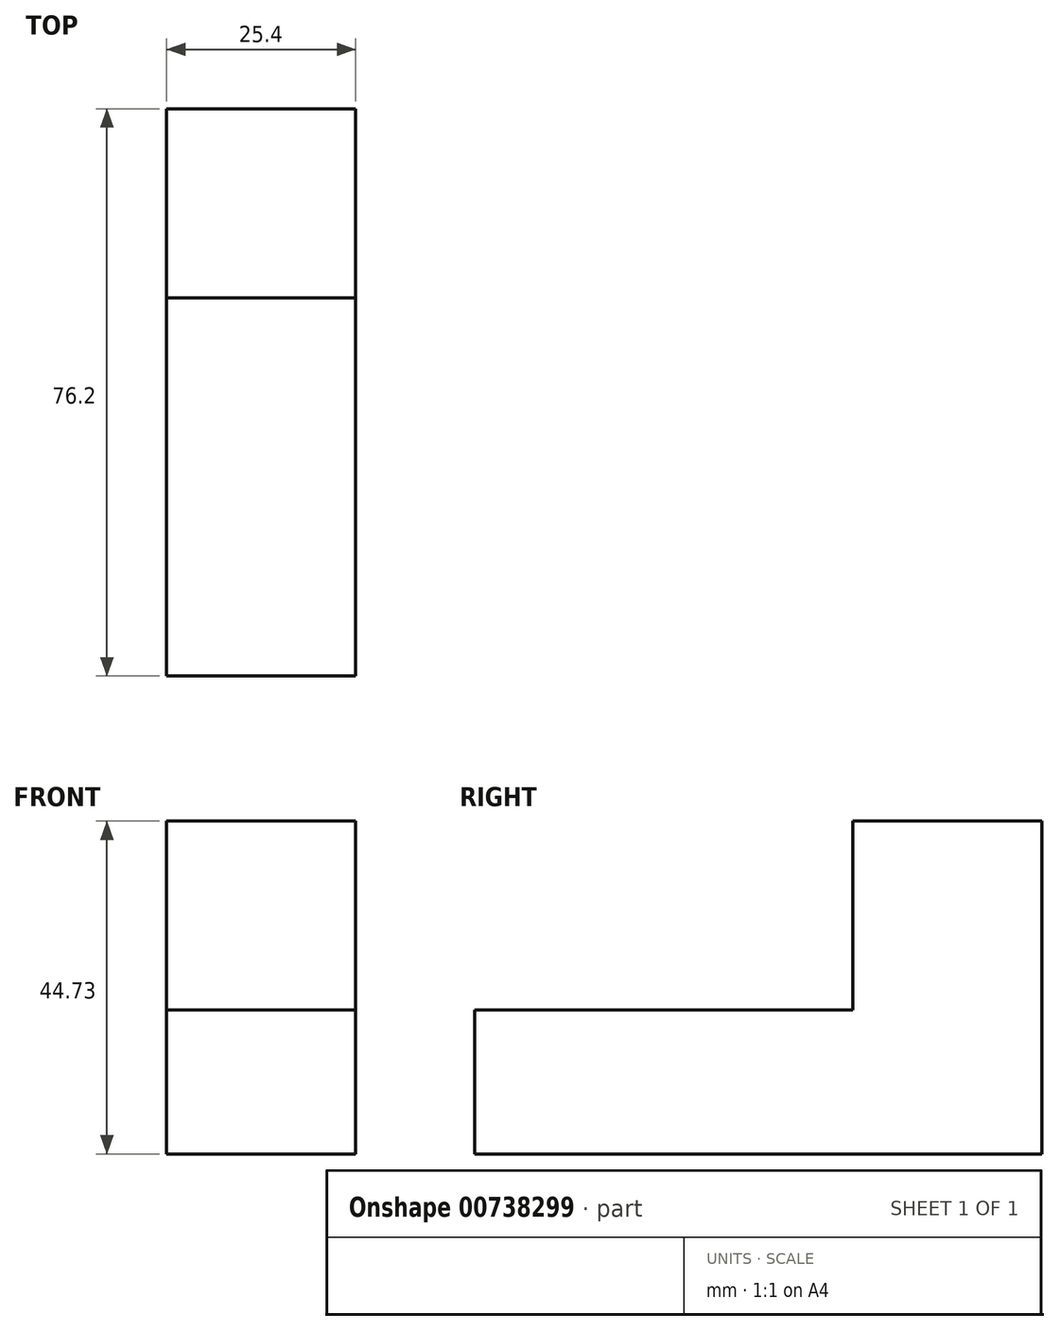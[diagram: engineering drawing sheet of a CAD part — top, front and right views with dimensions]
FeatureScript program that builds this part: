
annotation { "Feature Type Name" : "Feature", "Feature Type Description" : "" }
export const myFeature = defineFeature(function(context is Context, id is Id, definition is map)
    precondition{}
    {
        {
            var Q0;
            Q0=qCreatedBy(makeId("Right.planeOp"),FACE);
            var sketch = newSketch(context, id + "F0", { "sketchPlane" : qUnion([Q0])});
            skLineSegment(sketch, "E0", {"start": v(0, 0) * mm, "end": v(0, 44.73) * mm});
            skLineSegment(sketch, "E1", {"start": v(0, 44.73) * mm, "end": v(-25.4, 44.73) * mm});
            skLineSegment(sketch, "E2", {"start": v(-25.4, 44.73) * mm, "end": v(-25.4, 19.33) * mm});
            skLineSegment(sketch, "E3", {"start": v(-25.4, 19.33) * mm, "end": v(-76.2, 19.33) * mm});
            skLineSegment(sketch, "E4", {"start": v(-76.2, 19.33) * mm, "end": v(-76.2, 0) * mm});
            skLineSegment(sketch, "E5", {"start": v(-76.2, 0) * mm, "end": v(0, 0) * mm});
            skSolve(sketch);
        }
        {
            var Q0;
            Q0=makeQuery(id+"F0.imprint","IMPRINT",FACE,{"disambiguationData":[TD([[makeQuery(id+"F0.imprint","IMPRINT",EDGE,{"derivedFrom":sQuery(id+"F0.wireOp",EDGE,"E0")}),1.0]])]});
            extrude(context, id + "F1", {"entities" : qUnion([Q0]), "depth" : 25.4 * mm, "offsetDistance" : 25.4 * mm});
        }
    });
